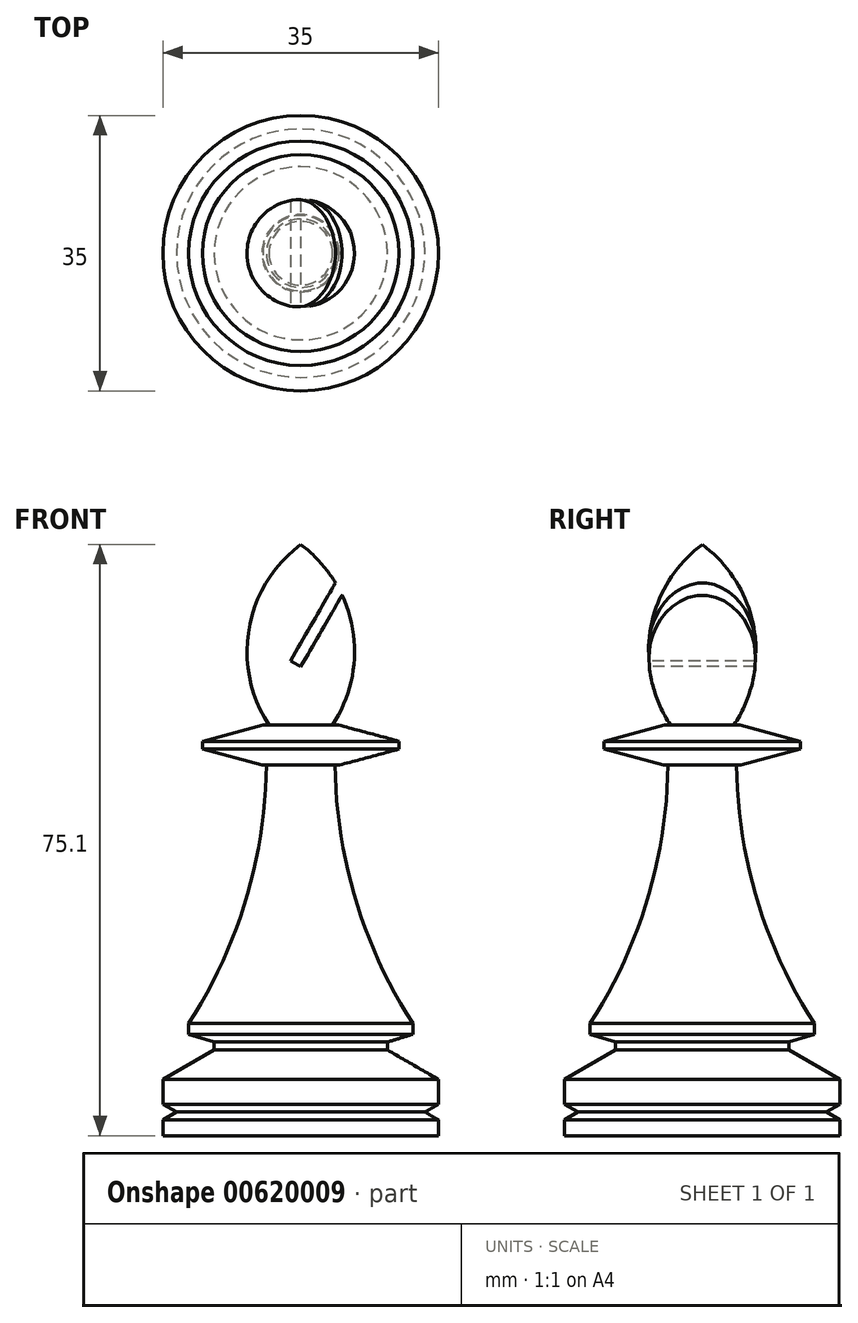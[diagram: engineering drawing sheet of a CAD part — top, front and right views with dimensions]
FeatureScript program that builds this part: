
annotation { "Feature Type Name" : "Feature", "Feature Type Description" : "" }
export const myFeature = defineFeature(function(context is Context, id is Id, definition is map)
    precondition{}
    {
        {
            var Q0;
            Q0=qCreatedBy(makeId("Front.planeOp"),FACE);
            var sketch = newSketch(context, id + "F0", { "sketchPlane" : qUnion([Q0])});
            skLineSegment(sketch, "E0", {"start": v(0, 0) * mm, "end": v(17.5, 0) * mm});
            skLineSegment(sketch, "E1", {"start": v(17.5, 0) * mm, "end": v(17.5, 2) * mm});
            skLineSegment(sketch, "E2", {"start": v(17.5, 7.13) * mm, "end": v(11, 10.89) * mm});
            skLineSegment(sketch, "E3", {"start": v(0, 14.4) * mm, "end": v(0, 0) * mm});
            skPoint(sketch, "E4.endSnap0", {"position": v(17.5, 3.57) * mm});
            skLineSegment(sketch, "E5", {"start": v(17.5, 2) * mm, "end": v(15.77, 3) * mm});
            skLineSegment(sketch, "E6", {"start": v(15.77, 3) * mm, "end": v(17.5, 4) * mm});
            skLineSegment(sketch, "E7.trimOffspring", {"start": v(17.5, 3.57) * mm, "end": v(17.5, 7.13) * mm});
            skLineSegment(sketch, "E8", {"start": v(11, 10.89) * mm, "end": v(11, 11.89) * mm});
            skLineSegment(sketch, "E9", {"start": v(11, 11.89) * mm, "end": v(14.25, 12.89) * mm});
            skLineSegment(sketch, "E10", {"start": v(14.25, 14.25) * mm, "end": v(14.25, 12.89) * mm});
            skLineSegment(sketch, "E11", {"start": v(0, 0) * mm, "end": v(0, 78) * mm});
            skArc(sketch, "E12", {"start": v(2.57, 74.16) * mm, "mid": v(1.37, 74.86) * mm, "end": v(0, 75.1) * mm});
            skPoint(sketch, "E13.first.point", {"position": v(2.57, 74.16) * mm});
            skPoint(sketch, "E13.third.point", {"position": v(10.83, 51.5) * mm});
            skLineSegment(sketch, "E14", {"start": v(12.5, 50.1) * mm, "end": v(12.5, 49.1) * mm});
            skLineSegment(sketch, "E15", {"start": v(12.5, 50.1) * mm, "end": v(4.8, 52.17) * mm});
            skLineSegment(sketch, "E16", {"start": v(12.5, 49.1) * mm, "end": v(4.92, 47.08) * mm});
            skLineSegment(sketch, "E17", {"start": v(4.05, 52.17) * mm, "end": v(4.8, 52.17) * mm});
            skArc(sketch, "E18", {"start": v(4.36, 47.09) * mm, "mid": v(6.97, 29.97) * mm, "end": v(14.25, 14.25) * mm});
            skPoint(sketch, "E18.first.point", {"position": v(4.36, 47.09) * mm});
            skPoint(sketch, "E18.second.point", {"position": v(75.46, -13.1) * mm});
            skPoint(sketch, "E18.third.point", {"position": v(14.25, 14.25) * mm});
            skPoint(sketch, "E19.orphan", {"position": v(0, 49.17) * mm});
            skPoint(sketch, "E20.start.orphan", {"position": v(0, 50.17) * mm});
            skLineSegment(sketch, "E21", {"start": v(0, 52.17) * mm, "end": v(0, 47.17) * mm});
            skLineSegment(sketch, "E22", {"start": v(4.92, 47.08) * mm, "end": v(4.36, 47.09) * mm});
            skArc(sketch, "E23", {"start": v(4.05, 52.17) * mm, "mid": v(6.57, 64.44) * mm, "end": v(0, 75.1) * mm});
            skPoint(sketch, "E23.second.point", {"position": v(-21.42, 48.8) * mm});
            skPoint(sketch, "E23.third.point", {"position": v(6.42, 65.18) * mm});
            skLineSegment(sketch, "E24", {"start": v(0, 75.1) * mm, "end": v(0, 0) * mm});
            skSolve(sketch);
        }
        {
            var Q0;
            {var subQ1=sQuery(id+"F0.wireOp",EDGE,"E0");Q0=makeQuery(id+"F0.imprint","IMPRINT",FACE,{"disambiguationData":[TD([[makeQuery(id+"F0.imprint","IMPRINT",EDGE,{"derivedFrom":subQ1}),1.0]])]});}
            var Q1;
            Q1=sQuery(id+"F0.wireOp",EDGE,"E3");
            revolve(context, id + "F1", {"entities" : qUnion([Q0]), "axis" : qUnion([Q1]), "revolveType" : RevolveType.FULL});
        }
        {
            var Q0;
            Q0=qCreatedBy(makeId("Front.planeOp"),FACE);
            var sketch = newSketch(context, id + "F2", { "sketchPlane" : qUnion([Q0])});
            skLineSegment(sketch, "E25", {"start": v(7.78, 73.05) * mm, "end": v(0, 59.58) * mm});
            skLineSegment(sketch, "E26", {"start": v(-25.93, 14.66) * mm, "end": v(-25.93, 70.38) * mm});
            skLineSegment(sketch, "E27.0", {"start": v(6.56, 73.94) * mm, "end": v(-1.3, 60.33) * mm});
            skLineSegment(sketch, "E28", {"start": v(0, 59.58) * mm, "end": v(-1.3, 60.33) * mm});
            skLineSegment(sketch, "E29", {"start": v(6.56, 73.94) * mm, "end": v(7.78, 73.05) * mm});
            skLineSegment(sketch, "E30", {"start": v(0, 59.58) * mm, "end": v(7.78, 73.05) * mm});
            skLineSegment(sketch, "E31", {"start": v(-1.3, 60.33) * mm, "end": v(6.56, 73.94) * mm});
            skLineSegment(sketch, "E32", {"start": v(-1.3, 60.33) * mm, "end": v(3.65, 68.9) * mm});
            skSolve(sketch);
        }
        {
            var Q0;
            Q0=qSketchRegion(id+"F2",true);
            extrude(context, id + "F3", {"entities" : qUnion([Q0]), "operationType" : NewBodyOperationType.REMOVE, "oppositeDirection" : true, "depth" : 50 * mm, "offsetDistance" : 25 * mm, "symmetric" : true});
        }
    });
